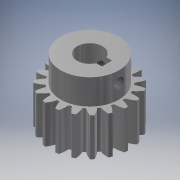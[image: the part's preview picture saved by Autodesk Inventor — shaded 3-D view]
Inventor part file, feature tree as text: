
AUTODESK INVENTOR PART (.ipt)
format: ipt  version: 2019 (Build 230136000, 136)  size: 282,112 bytes
history: native  units: mm (DEFAULTED — no unit token found)
features: sketch x7, extrude x6, plane x5, other x5
ambient origin geometry x8: Origin, YZ Plane, XZ Plane, XY Plane, X Axis, Y Axis, Z Axis, Center Point
bodies: Solid1 (feature_tree)
feature tree (23):
  extrude  "Extrusion1"  Depth=15.0mm TaperAngle=0.0deg
  plane  "Work Plane2"
  plane  "Work Plane8"
  plane  "Work Plane9"
  other  "正齒輪"
  extrude  "擠出2"  Depth=10.0mm TaperAngle=0.0deg
  extrude  "擠出3"  Depth=10.0mm
  extrude  "擠出4"  Depth=10.0mm TaperAngle=0.0deg
  plane  "工作平面11"
  extrude  "擠出5"  TaperAngle=0.0deg  [1 undecoded]
  plane  "工作平面12"
  extrude  "擠出6"  TaperAngle=0.0deg  [1 undecoded]
  other  "螺紋1"
  other  "螺紋2"
  sketch  "Sketch1"  dims[d0=31.5mm d1=15.0mm d2=0.0mm]
  sketch  "Sketch2"  dims[d3=28.5mm d4=10.0mm d5=0.0mm d16=57.0mm d17=0.0mm d34=1.65347mm d39=0.0mm d41=0.0mm d43=57.0mm d46=57.0mm d47=0.0mm d48=0.0mm d49=23.0mm d50=10.0mm d51=0.0mm d52=10.0mm d53=14.0mm d54=0.0mm d57=2.0mm d58=11.8mm d59=14.0mm d60=0.0mm d61=7.0mm d62=4.0mm d63=14.0mm d64=0.0mm d65=4.5mm d66=4.0mm d67=0.0mm d68=0.0mm d69=10.0mm d70=0.0mm d71=10.0mm d72=0.0mm]
  other  "Srf1"
  sketch  "草圖3"
  sketch  "草圖4"
  sketch  "草圖5"
  sketch  "草圖6"
  sketch  "草圖7"
  other  "節圓直徑"
note: 2 required parameter values undecoded (feature->parameter linkage not recoverable at this tier; creation-order binding heuristic only, values carry confidence <= 0.55)
